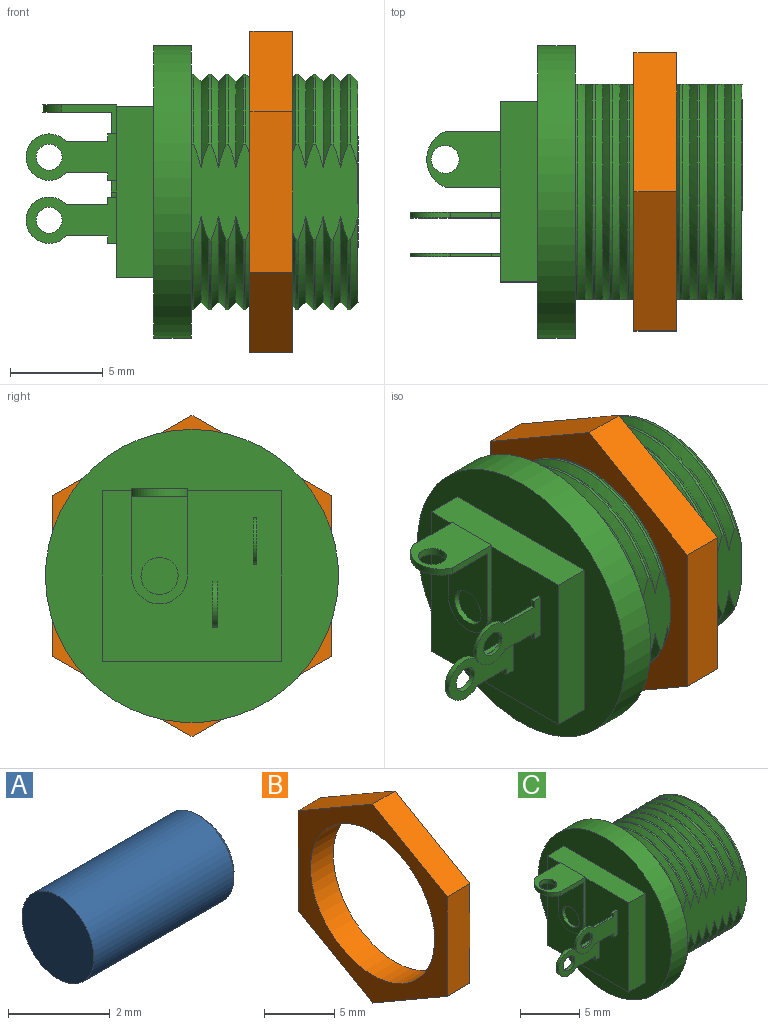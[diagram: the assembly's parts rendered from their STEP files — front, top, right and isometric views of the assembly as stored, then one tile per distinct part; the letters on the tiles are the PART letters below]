
ASSEMBLY  parts=3 mates=3
PART A: 4 faces, bbox 4x2x2 mm
  f0: cylinder r=1mm len=3.9mm, axis (-1,0,0), area 24.5mm2, adj f1,f3
  f1: cone r=0.9mm half-angle=45deg, axis (-1,0,0), area 0.8mm2, adj f0,f2
  f2: plane 1.8x1.8mm, normal (1,0,0), area 2.5mm2, adj f1
  f3: plane 2x2mm, normal (-1,0,0), area 3.1mm2, adj f0
PART B: 9 faces, bbox 2.3x15x17.3 mm
  f0: cylinder r=6.25mm len=12.5mm, axis (1,0,0), area 90.3mm2, adj f7,f8
  f1: plane 7.5x4.33mm, normal (0,0.5,0.87), area 19.9mm2, adj f2,f6,f7,f8
  f2: plane 8.66x2.3mm, normal (0,1,0), area 19.9mm2, adj f1,f3,f7,f8
  f3: plane 7.5x4.33mm, normal (0,0.5,-0.87), area 19.9mm2, adj f2,f4,f7,f8
  f4: plane 7.5x4.33mm, normal (0,-0.5,-0.87), area 19.9mm2, adj f3,f5,f7,f8
  f5: plane 8.66x2.3mm, normal (0,-1,0), area 19.9mm2, adj f4,f6,f7,f8
  f6: plane 7.5x4.33mm, normal (0,-0.5,0.87), area 19.9mm2, adj f1,f5,f7,f8
  f7: plane 17.32x15mm, normal (-1,0,0), area 72.1mm2, adj f0,f1,f2,f3,f4,f5,f6
  f8: plane 17.32x15mm, normal (1,0,0), area 72.1mm2, adj f0,f1,f2,f3,f4,f5,f6
PART C: 102 faces, bbox 18x15.9x15.9 mm
  f0: cylinder r=1.25mm len=2.5mm, axis (0,1,0), area 1.8mm2, adj f62,f64,f76,f77
  f1: cylinder r=1.25mm len=2.5mm, axis (0,1,0), area 1.2mm2, adj f58,f60,f80,f81
  f2: cylinder r=6.35mm len=11.6mm, axis (1,0,0), area 2mm2, adj f38,f71,f72,f99
  f3: cylinder r=6.35mm len=11.6mm, axis (1,0,0), area 2mm2, adj f36,f71,f72,f97
  f4: cylinder r=6.35mm len=11.6mm, axis (1,0,0), area 2mm2, adj f34,f71,f72,f95
  f5: cylinder r=6.35mm len=11.6mm, axis (1,0,0), area 2mm2, adj f32,f71,f72,f93
  f6: cylinder r=6.35mm len=11.6mm, axis (1,0,0), area 2mm2, adj f30,f71,f72,f91
  f7: cylinder r=6.35mm len=11.6mm, axis (1,0,0), area 2mm2, adj f28,f71,f72,f89
  f8: cylinder r=6.35mm len=11.6mm, axis (1,0,0), area 2mm2, adj f26,f71,f72,f87
  f9: cylinder r=6.35mm len=11.6mm, axis (1,0,0), area 2mm2, adj f24,f71,f72,f85
  f10: cylinder r=6.35mm len=11.6mm, axis (1,0,0), area 2mm2, adj f22,f71,f72,f83
  f11: cylinder r=6.35mm len=11.6mm, axis (1,0,0), area 2mm2, adj f52,f71,f72,f101
  f12: cylinder r=7.9mm len=15.8mm, axis (1,0,0), area 99.3mm2, adj f50,f52
  f13: cylinder r=1.62mm len=3mm, axis (0,0,-1), area 1.5mm2, adj f66,f67,f68,f69
  f14: cylinder r=0.75mm len=1.5mm, axis (0,0,-1), area 1.9mm2, adj f66,f68
  f15: cylinder r=3mm len=9mm, axis (1,0,0), area 169.6mm2, adj f51,f70
  f16: cylinder r=1.5mm len=3mm, axis (1,0,0), area 1.4mm2, adj f48,f67,f69,f73
  f17: cylinder r=1mm len=2mm, axis (1,0,0), area 1.9mm2, adj f73,f74
  f18: cylinder r=0.7mm len=1.4mm, axis (0,-1,0), area 1.3mm2, adj f62,f64
  f19: cylinder r=0.7mm len=1.4mm, axis (0,-1,0), area 0.9mm2, adj f58,f60
  f20: cone r=6.35mm half-angle=45deg, axis (-1,0,0), area 8.7mm2, adj f47,f51,f71,f72
  f21: cone r=6.35mm half-angle=45deg, axis (-1,0,0), area 8.7mm2, adj f46,f71,f72,f84
  f22: cone r=5.95mm half-angle=45deg, axis (1,0,0), area 8.7mm2, adj f10,f71,f72,f85
  f23: cone r=6.35mm half-angle=45deg, axis (-1,0,0), area 8.7mm2, adj f45,f71,f72,f86
  f24: cone r=5.95mm half-angle=45deg, axis (1,0,0), area 8.7mm2, adj f9,f71,f72,f87
  f25: cone r=6.35mm half-angle=45deg, axis (-1,0,0), area 8.7mm2, adj f44,f71,f72,f88
  f26: cone r=5.95mm half-angle=45deg, axis (1,0,0), area 8.7mm2, adj f8,f71,f72,f89
  f27: cone r=6.35mm half-angle=45deg, axis (-1,0,0), area 8.7mm2, adj f43,f71,f72,f90
  f28: cone r=5.95mm half-angle=45deg, axis (1,0,0), area 8.7mm2, adj f7,f71,f72,f91
  f29: cone r=6.35mm half-angle=45deg, axis (-1,0,0), area 8.7mm2, adj f42,f71,f72,f92
  f30: cone r=5.95mm half-angle=45deg, axis (1,0,0), area 8.7mm2, adj f6,f71,f72,f93
  f31: cone r=6.35mm half-angle=45deg, axis (-1,0,0), area 8.7mm2, adj f41,f71,f72,f94
  f32: cone r=5.95mm half-angle=45deg, axis (1,0,0), area 8.7mm2, adj f5,f71,f72,f95
  f33: cone r=6.35mm half-angle=45deg, axis (-1,0,0), area 8.7mm2, adj f40,f71,f72,f96
  f34: cone r=5.95mm half-angle=45deg, axis (1,0,0), area 8.7mm2, adj f4,f71,f72,f97
  f35: cone r=6.35mm half-angle=45deg, axis (-1,0,0), area 8.7mm2, adj f39,f71,f72,f98
  f36: cone r=5.95mm half-angle=45deg, axis (1,0,0), area 8.7mm2, adj f3,f71,f72,f99
  f37: cone r=6.35mm half-angle=45deg, axis (-1,0,0), area 8.7mm2, adj f49,f71,f72,f100
  f38: cone r=5.95mm half-angle=45deg, axis (1,0,0), area 8.7mm2, adj f2,f71,f72,f101
  f39: cylinder r=6.35mm len=11.6mm, axis (1,0,0), area 2mm2, adj f35,f71,f72,f100
  f40: cylinder r=6.35mm len=11.6mm, axis (1,0,0), area 2mm2, adj f33,f71,f72,f98
  f41: cylinder r=6.35mm len=11.6mm, axis (1,0,0), area 2mm2, adj f31,f71,f72,f96
  f42: cylinder r=6.35mm len=11.6mm, axis (1,0,0), area 2mm2, adj f29,f71,f72,f94
  f43: cylinder r=6.35mm len=11.6mm, axis (1,0,0), area 2mm2, adj f27,f71,f72,f92
  f44: cylinder r=6.35mm len=11.6mm, axis (1,0,0), area 2mm2, adj f25,f71,f72,f90
  f45: cylinder r=6.35mm len=11.6mm, axis (1,0,0), area 2mm2, adj f23,f71,f72,f88
  f46: cylinder r=6.35mm len=11.6mm, axis (1,0,0), area 2mm2, adj f21,f71,f72,f86
  f47: cylinder r=6.35mm len=11.6mm, axis (1,0,0), area 2mm2, adj f20,f71,f72,f84
  f48: plane 9.7x9.2mm, normal (-1,0,0), area 70.7mm2, adj f16,f53,f54,f55,f56,f57,f58,f59
  f49: cylinder r=6.35mm len=11.6mm, axis (1,0,0), area 2mm2, adj f37,f52,f71,f72
  f50: plane 15.8x15.8mm, normal (-1,0,0), area 106.8mm2, adj f12,f53,f54,f55,f56
  f51: plane 11.9x11.6mm, normal (1,0,0), area 82.4mm2, adj f15,f20,f71,f72,f83
  f52: plane 15.8x15.8mm, normal (1,0,0), area 73.2mm2, adj f11,f12,f49,f71,f72
  f53: plane 9.7x2mm, normal (0,0,-1), area 19.4mm2, adj f48,f50,f54,f56
  f54: plane 9.2x2mm, normal (0,-1,0), area 18.4mm2, adj f48,f50,f53,f55
  f55: plane 9.7x2mm, normal (0,0,1), area 19.4mm2, adj f48,f50,f54,f56,f65
  f56: plane 9.2x2mm, normal (0,1,0), area 18.4mm2, adj f48,f50,f53,f55
  f57: plane 0.5x0.2mm, normal (0,0,-1), area 0.1mm2, adj f48,f58,f60,f82
  f58: plane 4.9x2.5mm, normal (0,-1,0), area 8mm2, adj f1,f19,f48,f57,f59,f79,f80,f81
  f59: plane 0.5x0.2mm, normal (0,0,1), area 0.1mm2, adj f48,f58,f60,f79
  f60: plane 4.9x2.5mm, normal (0,1,0), area 8mm2, adj f1,f19,f48,f57,f59,f79,f80,f81
  f61: plane 0.5x0.3mm, normal (0,0,-1), area 0.2mm2, adj f48,f62,f64,f78
  f62: plane 4.9x2.5mm, normal (0,-1,0), area 8mm2, adj f0,f18,f48,f61,f63,f75,f76,f77
  f63: plane 0.5x0.3mm, normal (0,0,1), area 0.2mm2, adj f48,f62,f64,f75
  f64: plane 4.9x2.5mm, normal (0,1,0), area 8mm2, adj f0,f18,f48,f61,f63,f75,f76,f77
  f65: plane 3x0.1mm, normal (1,0,0), area 0.3mm2, adj f55,f67,f68,f69
  f66: plane 3.7x3mm, normal (0,0,-1), area 8.5mm2, adj f13,f14,f67,f69,f73
  f67: plane 4.7x3mm, normal (0,-1,0), area 2.5mm2, adj f13,f16,f48,f65,f66,f68,f73
  f68: plane 4x3mm, normal (0,0,1), area 9.4mm2, adj f13,f14,f65,f67,f69
  f69: plane 4.7x3mm, normal (0,1,0), area 2.5mm2, adj f13,f16,f48,f65,f66,f68,f73
  f70: plane 6x6mm, normal (1,0,0), area 28.3mm2, adj f15
  f71: plane 9.09x5.26mm, normal (0,1,0), area 37.9mm2, adj f2,f3,f4,f5,f6,f7,f8,f9
  f72: plane 9.09x5.26mm, normal (0,-1,0), area 37.9mm2, adj f2,f3,f4,f5,f6,f7,f8,f9
  f73: plane 5.8x3mm, normal (-1,0,0), area 13.3mm2, adj f16,f17,f66,f67,f69
  f74: plane 2x2mm, normal (-1,0,0), area 3.1mm2, adj f17
  f75: plane 0.4x0.3mm, normal (-1,0,0), area 0.1mm2, adj f62,f63,f64,f76
  f76: plane 2.23x0.3mm, normal (0,0,1), area 0.7mm2, adj f0,f62,f64,f75
  f77: plane 2.23x0.3mm, normal (0,0,-1), area 0.7mm2, adj f0,f62,f64,f78
  f78: plane 0.4x0.3mm, normal (-1,0,0), area 0.1mm2, adj f61,f62,f64,f77
  f79: plane 0.4x0.2mm, normal (-1,0,0), area 0.1mm2, adj f58,f59,f60,f80
  f80: plane 2.23x0.2mm, normal (0,0,1), area 0.4mm2, adj f1,f58,f60,f79
  f81: plane 2.23x0.2mm, normal (0,0,-1), area 0.4mm2, adj f1,f58,f60,f82
  f82: plane 0.4x0.2mm, normal (-1,0,0), area 0.1mm2, adj f57,f58,f60,f81
  f83: cone r=6.35mm half-angle=45deg, axis (-1,0,0), area 8.7mm2, adj f10,f51,f71,f72
  f84: cone r=5.95mm half-angle=45deg, axis (1,0,0), area 8.7mm2, adj f21,f47,f71,f72
  f85: cone r=6.35mm half-angle=45deg, axis (-1,0,0), area 8.7mm2, adj f9,f22,f71,f72
  f86: cone r=5.95mm half-angle=45deg, axis (1,0,0), area 8.7mm2, adj f23,f46,f71,f72
  f87: cone r=6.35mm half-angle=45deg, axis (-1,0,0), area 8.7mm2, adj f8,f24,f71,f72
  f88: cone r=5.95mm half-angle=45deg, axis (1,0,0), area 8.7mm2, adj f25,f45,f71,f72
  f89: cone r=6.35mm half-angle=45deg, axis (-1,0,0), area 8.7mm2, adj f7,f26,f71,f72
  f90: cone r=5.95mm half-angle=45deg, axis (1,0,0), area 8.7mm2, adj f27,f44,f71,f72
  f91: cone r=6.35mm half-angle=45deg, axis (-1,0,0), area 8.7mm2, adj f6,f28,f71,f72
  f92: cone r=5.95mm half-angle=45deg, axis (1,0,0), area 8.7mm2, adj f29,f43,f71,f72
  f93: cone r=6.35mm half-angle=45deg, axis (-1,0,0), area 8.7mm2, adj f5,f30,f71,f72
  f94: cone r=5.95mm half-angle=45deg, axis (1,0,0), area 8.7mm2, adj f31,f42,f71,f72
  f95: cone r=6.35mm half-angle=45deg, axis (-1,0,0), area 8.7mm2, adj f4,f32,f71,f72
  f96: cone r=5.95mm half-angle=45deg, axis (1,0,0), area 8.7mm2, adj f33,f41,f71,f72
  f97: cone r=6.35mm half-angle=45deg, axis (-1,0,0), area 8.7mm2, adj f3,f34,f71,f72
  f98: cone r=5.95mm half-angle=45deg, axis (1,0,0), area 8.7mm2, adj f35,f40,f71,f72
  f99: cone r=6.35mm half-angle=45deg, axis (-1,0,0), area 8.7mm2, adj f2,f36,f71,f72
  f100: cone r=5.95mm half-angle=45deg, axis (1,0,0), area 8.7mm2, adj f37,f39,f71,f72
  f101: cone r=6.35mm half-angle=45deg, axis (-1,0,0), area 8.7mm2, adj f11,f38,f71,f72
PLACE A t=(-6.3,5.8,0)mm
PLACE B t=(-5.32,5.8,0)mm
PLACE C t=(-6.8,5.8,0)mm
MATE cylindrical A.f0 <-> C.f15  axis (-1,0,0) through (-11.3,7.8,0)mm
MATE cylindrical B.f0 <-> C.f2  axis (1,0,0) through (-11.48,5.8,0)mm
MATE planar C.f52 <-> B.f0  axis (1,0,0) through (-15.8,0,0)mm
